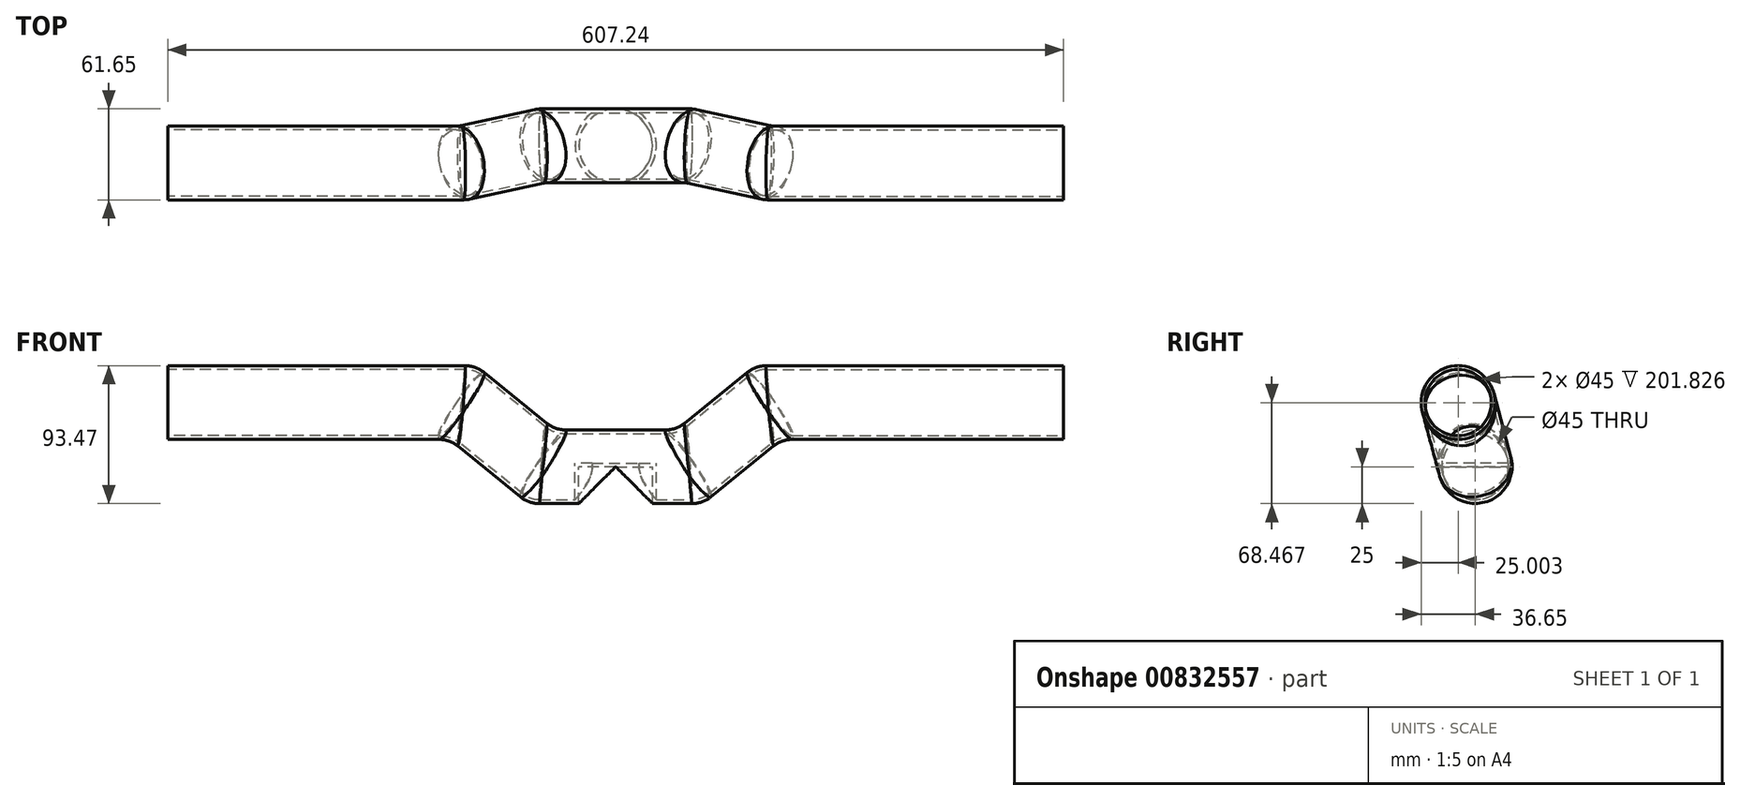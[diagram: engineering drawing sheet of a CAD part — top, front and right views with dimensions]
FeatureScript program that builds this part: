
annotation { "Feature Type Name" : "Feature", "Feature Type Description" : "" }
export const myFeature = defineFeature(function(context is Context, id is Id, definition is map)
    precondition{}
    {
        {
            var Q0;
            Q0=qCreatedBy(makeId("Top.planeOp"),FACE);
            var sketch = newSketch(context, id + "F0", { "sketchPlane" : qUnion([Q0])});
            skLineSegment(sketch, "E0", {"start": v(-40.27, 0) * mm, "end": v(42.35, 0) * mm});
            skSolve(sketch);
        }
        {
            var Q0;
            Q0=sQuery(id+"F0.wireOp",EDGE,"E0");
            cPlane(context, id + "F1", {"entities" : qUnion([Q0]), "cplaneType" : CPlaneType.LINE_ANGLE, "offset" : 25 * mm, "angle" : 15 * degree, "width" : 150 * mm, "height" : 150 * mm});
        }
        {
            var Q0;
            Q0=qCreatedBy(id+"F1.planeOp",FACE);
            var sketch = newSketch(context, id + "F2", { "sketchPlane" : qUnion([Q0])});
            skLineSegment(sketch, "E1", {"start": v(0, 0) * mm, "end": v(-50, 0) * mm});
            skLineSegment(sketch, "E2", {"start": v(-50, 0) * mm, "end": v(-103.62, 45) * mm});
            skLineSegment(sketch, "E3", {"start": v(-103.62, 45) * mm, "end": v(-303.62, 45) * mm});
            skSolve(sketch);
        }
        {
            var Q0;
            Q0=qCreatedBy(makeId("Right.planeOp"),FACE);
            var sketch = newSketch(context, id + "F3", { "sketchPlane" : qUnion([Q0])});
            skCircle(sketch, "E4", {"center": v(0, 0) * mm, "radius": 25 * mm});
            skSolve(sketch);
        }
        {
            var Q0;
            Q0=makeQuery(id+"F3.imprint","IMPRINT",FACE,{"disambiguationData":[TD([[makeQuery(id+"F3.imprint","IMPRINT",EDGE,{"derivedFrom":sQuery(id+"F3.wireOp",EDGE,"E4")}),1.0]])]});
            var Q1;
            Q1=sQuery(id+"F2.wireOp",EDGE,"E1");
            var Q2;
            Q2=sQuery(id+"F2.wireOp",EDGE,"E2");
            var Q3;
            Q3=sQuery(id+"F2.wireOp",EDGE,"E3");
            sweep(context, id + "F4", {"profiles" : qUnion([Q0]), "path" : qUnion([Q1, Q2, Q3])});
        }
        {
            var Q0;
            Q0=makeQuery(id+"F4.opSweep","SWEPT_BODY",BODY,{"disambiguationData":[OSD([sQuery(id+"F2.wireOp",EDGE,"E3"),sQuery(id+"F3.wireOp",EDGE,"E4")])]});
            var Q1;
            Q1=qCreatedBy(makeId("Right.planeOp"),FACE);
            mirror(context, id + "F5", {"operationType" : NewBodyOperationType.ADD, "entities" : qUnion([Q0]), "mirrorPlane" : qUnion([Q1])});
        }
        {
            var Q0;
            Q0=qCreatedBy(makeId("Top.planeOp"),FACE);
            var sketch = newSketch(context, id + "F6", { "sketchPlane" : qUnion([Q0])});
            skCircle(sketch, "E5", {"center": v(0, 0) * mm, "radius": 25 * mm});
            skSolve(sketch);
        }
        {
            var Q0;
            Q0 = qSketchRegion(id + "F6", true);
            extrude(context, id + "F7", {"entities" : qUnion([Q0]), "operationType" : NewBodyOperationType.REMOVE, "endBound" : BoundingType.UP_TO_NEXT, "oppositeDirection" : true, "depth" : 25 * mm, "offsetDistance" : 25 * mm});
        }
        {
            var Q0;
            Q0=makeQuery(id+"F4.opSweep","MID_CAP_EDGE",EDGE,{"disambiguationData":[OSD([sQuery(id+"F2.wireOp",VERTEX,"E3.start"),sQuery(id+"F3.wireOp",EDGE,"E4")])],"capPos":2.0});
            var Q1;
            Q1=makeQuery(id+"F4.opSweep","MID_CAP_EDGE",EDGE,{"disambiguationData":[OSD([sQuery(id+"F2.wireOp",VERTEX,"E2.start"),sQuery(id+"F3.wireOp",EDGE,"E4")])],"capPos":1.0});
            fillet(context, id + "F8", {"entities" : qUnion([Q0, Q1]), "radius" : 20 * mm, "tangentPropagation" : true, "allowEdgeOverflow" : false});
        }
        {
            var Q0;
            Q0=makeQuery(id+"F5.opPattern","COPY",EDGE,{"derivedFrom":makeQuery(id+"F4.opSweep","MID_CAP_EDGE",EDGE,{"disambiguationData":[OSD([sQuery(id+"F2.wireOp",VERTEX,"E2.start"),sQuery(id+"F3.wireOp",EDGE,"E4")])],"capPos":1.0}),"instanceName":"1"});
            var Q1;
            Q1=makeQuery(id+"F5.opPattern","COPY",EDGE,{"derivedFrom":makeQuery(id+"F4.opSweep","MID_CAP_EDGE",EDGE,{"disambiguationData":[OSD([sQuery(id+"F2.wireOp",VERTEX,"E3.start"),sQuery(id+"F3.wireOp",EDGE,"E4")])],"capPos":2.0}),"instanceName":"1"});
            fillet(context, id + "F9", {"entities" : qUnion([Q0, Q1]), "radius" : 20 * mm, "tangentPropagation" : true, "allowEdgeOverflow" : false});
        }
        {
            var Q0;
            Q0=makeQuery(id+"F4.opSweep","CAP_FACE",FACE,{"disambiguationData":[OSD([sQuery(id+"F2.wireOp",VERTEX,"E3.end"),sQuery(id+"F3.wireOp",EDGE,"E4")])],"isStart":false});
            var Q1;
            Q1=makeQuery(id+"F5.opPattern","COPY",FACE,{"derivedFrom":makeQuery(id+"F4.opSweep","CAP_FACE",FACE,{"disambiguationData":[OSD([sQuery(id+"F2.wireOp",VERTEX,"E3.end"),sQuery(id+"F3.wireOp",EDGE,"E4")])],"isStart":false}),"instanceName":"1"});
            shell(context, id + "F10", {"entities" : qUnion([Q0, Q1]), "thickness" : 2.5 * mm});
        }
    });
